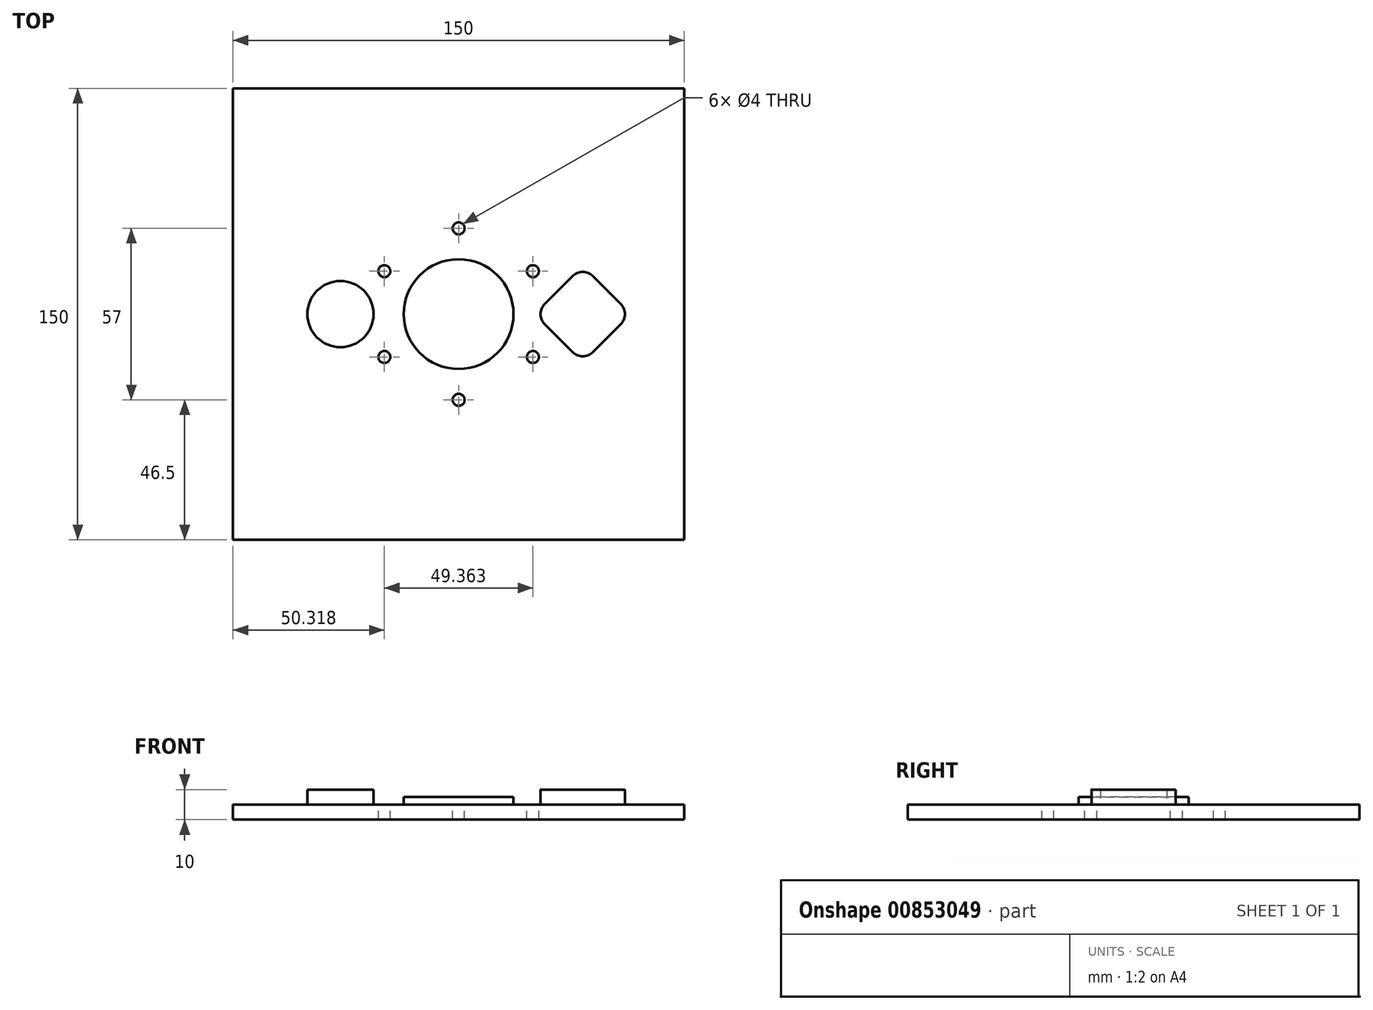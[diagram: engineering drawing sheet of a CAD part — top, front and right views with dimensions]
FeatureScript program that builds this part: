
annotation { "Feature Type Name" : "Feature", "Feature Type Description" : "" }
export const myFeature = defineFeature(function(context is Context, id is Id, definition is map)
    precondition{}
    {
        {
            var Q0;
            Q0=qCreatedBy(makeId("Top.planeOp"),FACE);
            var sketch = newSketch(context, id + "F0", { "sketchPlane" : qUnion([Q0])});
            skLineSegment(sketch, "E0.bottom", {"start": v(75, -75) * mm, "end": v(-75, -75) * mm});
            skLineSegment(sketch, "E0.top", {"start": v(75, 75) * mm, "end": v(-75, 75) * mm});
            skLineSegment(sketch, "E0.left", {"start": v(75, -75) * mm, "end": v(75, 75) * mm});
            skLineSegment(sketch, "E0.right", {"start": v(-75, -75) * mm, "end": v(-75, 75) * mm});
            skPoint(sketch, "E0.middle", {"position": v(0, 0) * mm});
            skSolve(sketch);
        }
        {
            var Q0;
            Q0 = qSketchRegion(id + "F0", true);
            extrude(context, id + "F1", {"entities" : qUnion([Q0]), "oppositeDirection" : true, "depth" : 5 * mm, "offsetDistance" : 25 * mm});
        }
        {
            var Q0;
            Q0=makeQuery(id+"F1.opExtrude","CAP_FACE",FACE,{"disambiguationData":[OSD([sQuery(id+"F0.wireOp",EDGE,"E0.bottom"),sQuery(id+"F0.wireOp",EDGE,"E0.top"),sQuery(id+"F0.wireOp",EDGE,"E0.left"),sQuery(id+"F0.wireOp",EDGE,"E0.right")])],"isStart":true});
            var sketch = newSketch(context, id + "F2", { "sketchPlane" : qUnion([Q0])});
            skCircle(sketch, "E1", {"center": v(0, 0) * mm, "radius": 18.25 * mm});
            skSolve(sketch);
        }
        {
            var Q0;
            Q0 = qSketchRegion(id + "F2", true);
            extrude(context, id + "F3", {"entities" : qUnion([Q0]), "operationType" : NewBodyOperationType.ADD, "depth" : 2.5 * mm, "offsetDistance" : 25 * mm});
        }
        {
            var Q0;
            Q0=makeQuery(id+"F1.opExtrude","CAP_FACE",FACE,{"disambiguationData":[OSD([sQuery(id+"F0.wireOp",EDGE,"E0.bottom"),sQuery(id+"F0.wireOp",EDGE,"E0.top"),sQuery(id+"F0.wireOp",EDGE,"E0.left"),sQuery(id+"F0.wireOp",EDGE,"E0.right")])],"isStart":true});
            var sketch = newSketch(context, id + "F4", { "sketchPlane" : qUnion([Q0])});
            skLineSegment(sketch, "E2", {"start": v(0, 0) * mm, "end": v(-39.25, 0) * mm, "construction": true});
            skCircle(sketch, "E3", {"center": v(-39.25, 0) * mm, "radius": 11 * mm});
            skLineSegment(sketch, "E4", {"start": v(0, 0) * mm, "end": v(41.25, 0) * mm, "construction": true});
            skCircle(sketch, "E5", {"center": v(41.25, 0) * mm, "radius": 14 * mm, "construction": true});
            skArc(sketch, "E6", {"start": v(28.71, 3.54) * mm, "mid": v(27.25, 0) * mm, "end": v(28.71, -3.54) * mm});
            skArc(sketch, "E7.1.0", {"start": v(37.71, -12.54) * mm, "mid": v(41.25, -14) * mm, "end": v(44.79, -12.54) * mm});
            skArc(sketch, "E7.2.0", {"start": v(53.79, -3.54) * mm, "mid": v(55.25, 0) * mm, "end": v(53.79, 3.54) * mm});
            skArc(sketch, "E7.3.0", {"start": v(44.79, 12.54) * mm, "mid": v(41.25, 14) * mm, "end": v(37.71, 12.54) * mm});
            skLineSegment(sketch, "E8", {"start": v(28.71, 3.54) * mm, "end": v(37.71, 12.54) * mm});
            skLineSegment(sketch, "E9", {"start": v(44.79, 12.54) * mm, "end": v(53.79, 3.54) * mm});
            skLineSegment(sketch, "E10", {"start": v(53.79, -3.54) * mm, "end": v(44.79, -12.54) * mm});
            skLineSegment(sketch, "E11", {"start": v(28.71, -3.54) * mm, "end": v(37.71, -12.54) * mm});
            skSolve(sketch);
        }
        {
            var Q0;
            Q0 = qSketchRegion(id + "F4", true);
            extrude(context, id + "F5", {"entities" : qUnion([Q0]), "operationType" : NewBodyOperationType.ADD, "depth" : 5 * mm, "offsetDistance" : 25 * mm});
        }
        {
            var Q0;
            Q0=makeQuery(id+"F1.opExtrude","CAP_FACE",FACE,{"disambiguationData":[OSD([sQuery(id+"F0.wireOp",EDGE,"E0.bottom"),sQuery(id+"F0.wireOp",EDGE,"E0.top"),sQuery(id+"F0.wireOp",EDGE,"E0.left"),sQuery(id+"F0.wireOp",EDGE,"E0.right")])],"isStart":true});
            var sketch = newSketch(context, id + "F6", { "sketchPlane" : qUnion([Q0])});
            skCircle(sketch, "E12", {"center": v(0, 0) * mm, "radius": 28.5 * mm, "construction": true});
            skLineSegment(sketch, "E13", {"start": v(0, 0) * mm, "end": v(0, 28.5) * mm, "construction": true});
            skCircle(sketch, "E14", {"center": v(0, 28.5) * mm, "radius": 2 * mm});
            skCircle(sketch, "E15.1.0", {"center": v(-24.68, 14.25) * mm, "radius": 2 * mm});
            skCircle(sketch, "E15.2.0", {"center": v(-24.68, -14.25) * mm, "radius": 2 * mm});
            skCircle(sketch, "E15.3.0", {"center": v(0, -28.5) * mm, "radius": 2 * mm});
            skCircle(sketch, "E15.4.0", {"center": v(24.68, -14.25) * mm, "radius": 2 * mm});
            skCircle(sketch, "E15.5.0", {"center": v(24.68, 14.25) * mm, "radius": 2 * mm});
            skLineSegment(sketch, "E16", {"start": v(0, 0) * mm, "end": v(24.68, 14.25) * mm, "construction": true});
            skSolve(sketch);
        }
        {
            var Q0;
            Q0 = qSketchRegion(id + "F6", true);
            extrude(context, id + "F7", {"entities" : qUnion([Q0]), "operationType" : NewBodyOperationType.REMOVE, "endBound" : BoundingType.THROUGH_ALL, "oppositeDirection" : true, "depth" : 25 * mm, "offsetDistance" : 25 * mm});
        }
    });
